# Revit family: Estrichüberdecktes Kanalsystem EÜK_Unterflur-Installationskanal_3-zügig
name_source: partatom
category: Generic Models
revit_build: Autodesk Revit 2015 (Build: 20140606_1530(x64)
units: mm (PartAtom-declared; Revit-internal decimal feet)

## types (6) — shared parameters
Manufacturer = OBO Bettermann
Material = Steel, Galvanized
URL = http://www.obo-bettermann.com

## per-type parameters (varying)
| type | GTIN | Manufacturer Art. No. | Size "a" | Size "b" | Width |
| S3 25028 | 4012195089339 | 7400324 | 90 mm  [stored 0.295276 ft] | 70 mm  [stored 0.229659 ft] | 250 mm  [stored 0.82021 ft] |
| S3 35028 | 4012195089384 | 7400336 | 120 mm  [stored 0.393701 ft] | 110 mm  [stored 0.360892 ft] | 350 mm  [stored 1.14829 ft] |
| S3 25038 | 4012195089346 | 7400328 | 90 mm  [stored 0.295276 ft] | 70 mm  [stored 0.229659 ft] | 250 mm  [stored 0.82021 ft] |
| S3 25048 | 4012195089377 | 7400332 | 90 mm  [stored 0.295276 ft] | 70 mm  [stored 0.229659 ft] | 250 mm  [stored 0.82021 ft] |
| S3 35038 | 4012195089391 | 7400340 | 120 mm  [stored 0.393701 ft] | 110 mm  [stored 0.360892 ft] | 350 mm  [stored 1.14829 ft] |
| S3 35048 | 4012195089407 | 7400344 | 120 mm  [stored 0.393701 ft] | 110 mm  [stored 0.360892 ft] | 350 mm  [stored 1.14829 ft] |

note: column(s) folded — value = type name in every type: Article Type

note: [stored X ft] marks values corroborated as IEEE doubles in the binary element streams (Revit-internal decimal feet)

## geometry (parser evidence)
native form markers: Sweep x2
no freeform markers — native parametric forms only
